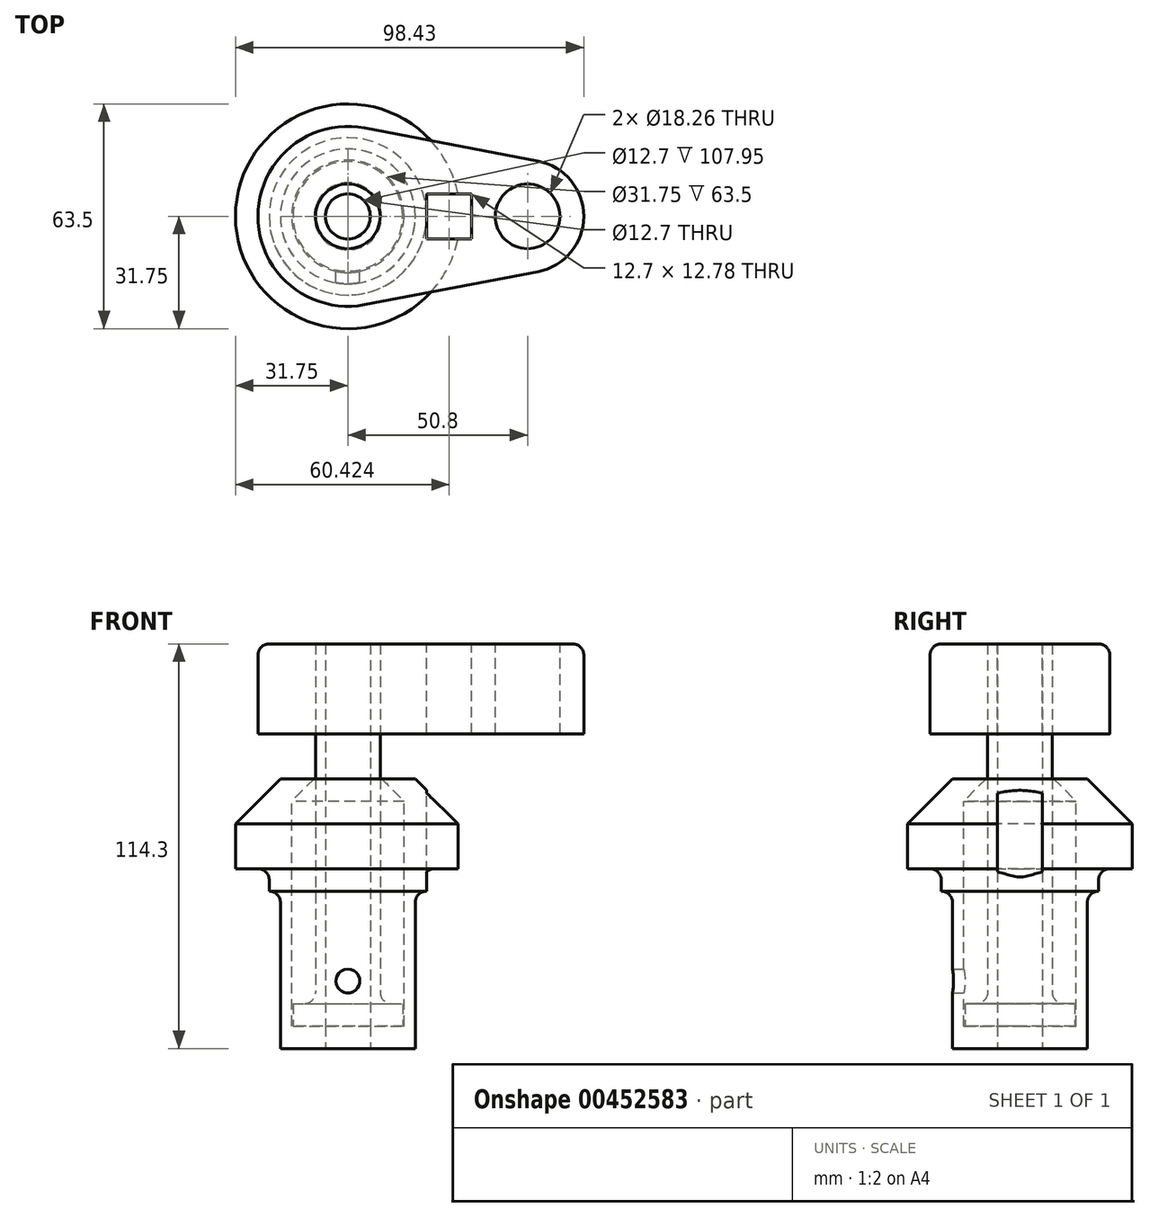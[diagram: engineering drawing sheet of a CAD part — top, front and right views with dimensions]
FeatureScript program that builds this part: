
annotation { "Feature Type Name" : "Feature", "Feature Type Description" : "" }
export const myFeature = defineFeature(function(context is Context, id is Id, definition is map)
    precondition{}
    {
        {
            var Q0;
            Q0=qCreatedBy(makeId("Front.planeOp"),FACE);
            var sketch = newSketch(context, id + "F0", { "sketchPlane" : qUnion([Q0])});
            skLineSegment(sketch, "E0", {"start": v(0, 0) * mm, "end": v(0, 76.2) * mm});
            skLineSegment(sketch, "E1", {"start": v(0, 76.2) * mm, "end": v(19.05, 76.2) * mm});
            skLineSegment(sketch, "E2", {"start": v(19.05, 76.2) * mm, "end": v(31.75, 63.5) * mm});
            skLineSegment(sketch, "E3", {"start": v(31.75, 63.5) * mm, "end": v(31.75, 50.8) * mm});
            skLineSegment(sketch, "E4", {"start": v(31.75, 50.8) * mm, "end": v(22.23, 50.8) * mm});
            skLineSegment(sketch, "E5", {"start": v(22.23, 50.8) * mm, "end": v(22.23, 44.45) * mm});
            skLineSegment(sketch, "E6", {"start": v(22.23, 44.45) * mm, "end": v(19.05, 44.45) * mm});
            skLineSegment(sketch, "E7", {"start": v(19.05, 44.45) * mm, "end": v(19.05, 0) * mm});
            skLineSegment(sketch, "E8", {"start": v(19.05, 0) * mm, "end": v(0, 0) * mm});
            skLineSegment(sketch, "E9", {"start": v(9.52, 76.2) * mm, "end": v(15.88, 69.85) * mm});
            skLineSegment(sketch, "E10", {"start": v(15.88, 69.85) * mm, "end": v(15.88, 6.35) * mm});
            skLineSegment(sketch, "E11", {"start": v(15.88, 6.35) * mm, "end": v(0, 6.35) * mm});
            skLineSegment(sketch, "E12", {"start": v(0, 76.2) * mm, "end": v(0, 96.2) * mm, "construction": true});
            skLineSegment(sketch, "E13", {"start": v(0, 76.2) * mm, "end": v(0, 114.3) * mm});
            skLineSegment(sketch, "E14", {"start": v(0, 114.3) * mm, "end": v(9.13, 114.3) * mm});
            skLineSegment(sketch, "E15", {"start": v(9.13, 114.3) * mm, "end": v(9.13, 12.7) * mm});
            skLineSegment(sketch, "E16", {"start": v(9.13, 12.7) * mm, "end": v(15.48, 12.7) * mm});
            skLineSegment(sketch, "E17", {"start": v(15.48, 12.7) * mm, "end": v(15.48, 6.35) * mm});
            skSolve(sketch);
        }
        {
            var Q0;
            {var subQ4=sQuery(id+"F0.wireOp",EDGE,"E2");Q0=makeQuery(id+"F0.imprint","IMPRINT",FACE,{"disambiguationData":[TD([[makeQuery(id+"F0.imprint","IMPRINT",EDGE,{"derivedFrom":subQ4}),-1.0]])]});}
            var Q1;
            Q1=sQuery(id+"F0.wireOp",EDGE,"E0");
            revolve(context, id + "F1", {"entities" : qUnion([Q0]), "axis" : qUnion([Q1]), "revolveType" : RevolveType.FULL, "oppositeDirection" : true});
        }
        {
            var Q0;
            {var subQ0=sQuery(id+"F0.wireOp",EDGE,"E13");Q0=makeQuery(id+"F0.imprint","IMPRINT",FACE,{"disambiguationData":[TD([[makeQuery(id+"F0.imprint","IMPRINT",EDGE,{"derivedFrom":subQ0}),-1.0]])]});}
            var Q1;
            {var subQ0=sQuery(id+"F0.wireOp",EDGE,"E16");Q1=makeQuery(id+"F0.imprint","IMPRINT",FACE,{"disambiguationData":[TD([[makeQuery(id+"F0.imprint","IMPRINT",EDGE,{"derivedFrom":subQ0}),-1.0]])]});}
            var Q2;
            Q2=sQuery(id+"F0.wireOp",EDGE,"E13");
            revolve(context, id + "F2", {"entities" : qUnion([Q0, Q1]), "axis" : qUnion([Q2]), "revolveType" : RevolveType.FULL});
        }
        {
            var Q0;
            Q0=makeQuery(id+"F2.opRevolve","SWEPT_FACE",FACE,{"disambiguationData":[OSD([sQuery(id+"F0.wireOp",EDGE,"E14")])]});
            var sketch = newSketch(context, id + "F3", { "sketchPlane" : qUnion([Q0])});
            skCircle(sketch, "E18", {"center": v(0, 0) * mm, "radius": 25.4 * mm});
            skCircle(sketch, "E19", {"center": v(50.8, 0) * mm, "radius": 15.88 * mm});
            skLineSegment(sketch, "E20", {"start": v(53.78, 15.6) * mm, "end": v(4.76, 24.95) * mm});
            skLineSegment(sketch, "E21", {"start": v(4.76, -24.95) * mm, "end": v(53.78, -15.6) * mm});
            skCircle(sketch, "E22.0", {"center": v(0, 0) * mm, "radius": 9.13 * mm});
            skCircle(sketch, "E23", {"center": v(50.8, 0) * mm, "radius": 9.13 * mm});
            skSolve(sketch);
        }
        {
            var Q0;
            Q0 = qSketchRegion(id + "F3", true);
            var Q1;
            Q1=makeQuery(id+"F1.opRevolve","SWEPT_FACE",FACE,{"disambiguationData":[OSD([sQuery(id+"F0.wireOp",EDGE,"E1")])]});
            extrude(context, id + "F4", {"entities" : qUnion([Q0]), "oppositeDirection" : true, "endBoundEntityFace" : qUnion([Q1]), "depth" : 25.4 * mm});
        }
        {
            var Q0;
            Q0=qCreatedBy(makeId("Front.planeOp"),FACE);
            var sketch = newSketch(context, id + "F5", { "sketchPlane" : qUnion([Q0])});
            skPoint(sketch, "E24", {"position": v(0, 19.05) * mm});
            skSolve(sketch);
        }
        {
            var Q0;
            Q0=sQuery(id+"F5.wireOp",VERTEX,"E24");
            var Q1;
            Q1=makeQuery(id+"F1.opRevolve","SWEPT_BODY",BODY,{"disambiguationData":[OSD([sQuery(id+"F0.wireOp",EDGE,"E0"),sQuery(id+"F0.wireOp",EDGE,"E1"),sQuery(id+"F0.wireOp",EDGE,"E2"),sQuery(id+"F0.wireOp",EDGE,"E3"),sQuery(id+"F0.wireOp",EDGE,"E4"),sQuery(id+"F0.wireOp",EDGE,"E5"),sQuery(id+"F0.wireOp",EDGE,"E6"),sQuery(id+"F0.wireOp",EDGE,"E7"),sQuery(id+"F0.wireOp",EDGE,"E8"),sQuery(id+"F0.wireOp",EDGE,"E9"),sQuery(id+"F0.wireOp",EDGE,"E10"),sQuery(id+"F0.wireOp",EDGE,"E11")])]});
            hole(context, id + "F6", {"style" : HoleStyle.SIMPLE, "endStyle" : HoleEndStyle.THROUGH, "oppositeDirection" : true, "standardTappedOrClearance" : lookupTablePath({ "standard" : "ANSI", "fit" : "Normal (ASME)", "size" : "1/4", "type" : "Clearance" }), "standardBlindInLast" : lookupTablePath({ "fit" : "Free", "standard" : "ANSI", "size" : "1/4", "type" : "Clearance" }), "holeDiameter" : 6.76 * mm, "tappedDepth" : 14.3 * mm, "tapClearance" : 3, "locations" : qUnion([Q0]), "scope" : qUnion([Q1])});
        }
        {
            var Q0;
            Q0=makeQuery(id+"F4.opExtrude","CAP_EDGE",EDGE,{"disambiguationData":[OSD([sQuery(id+"F3.wireOp",EDGE,"E20")])],"isStart":true});
            var Q1;
            Q1=makeQuery(id+"F1.opRevolve","SWEPT_EDGE",EDGE,{"disambiguationData":[OSD([sQuery(id+"F0.wireOp",EDGE,"E6"),sQuery(id+"F0.wireOp",EDGE,"E7")])]});
            var Q2;
            Q2=makeQuery(id+"F1.opRevolve","SWEPT_EDGE",EDGE,{"disambiguationData":[OSD([sQuery(id+"F0.wireOp",EDGE,"E4"),sQuery(id+"F0.wireOp",EDGE,"E5")])]});
            var Q3;
            Q3=makeQuery(id+"F2.opRevolve","SWEPT_EDGE",EDGE,{"disambiguationData":[OSD([sQuery(id+"F0.wireOp",EDGE,"E15"),sQuery(id+"F0.wireOp",EDGE,"E16")])]});
            fillet(context, id + "F7", {"entities" : qUnion([Q0, Q1, Q2, Q3]), "radius" : 3.17 * mm, "tangentPropagation" : true, "allowEdgeOverflow" : false});
        }
        {
            var Q0;
            Q0=makeQuery(id+"F1.opRevolve","SWEPT_FACE",FACE,{"disambiguationData":[OSD([sQuery(id+"F0.wireOp",EDGE,"E8")])]});
            var sketch = newSketch(context, id + "F8", { "sketchPlane" : qUnion([Q0])});
            skCircle(sketch, "E25", {"center": v(0, 0) * mm, "radius": 6.35 * mm});
            skSolve(sketch);
        }
        {
            var Q0;
            Q0=makeQuery(id+"F8.imprint","IMPRINT",FACE,{"disambiguationData":[TD([[makeQuery(id+"F8.imprint","IMPRINT",EDGE,{"derivedFrom":sQuery(id+"F8.wireOp",EDGE,"E25")}),1.0]])]});
            extrude(context, id + "F9", {"entities" : qUnion([Q0]), "operationType" : NewBodyOperationType.REMOVE, "endBound" : BoundingType.THROUGH_ALL, "oppositeDirection" : true, "depth" : 25.4 * mm});
        }
        {
            var Q0;
            Q0=makeQuery(id+"F4.opExtrude","CAP_FACE",FACE,{"disambiguationData":[OSD([sQuery(id+"F3.wireOp",EDGE,"E18"),sQuery(id+"F3.wireOp",EDGE,"E19"),sQuery(id+"F3.wireOp",EDGE,"E20"),sQuery(id+"F3.wireOp",EDGE,"E21"),sQuery(id+"F3.wireOp",EDGE,"E22.0"),sQuery(id+"F3.wireOp",EDGE,"E23")])],"isStart":true});
            var sketch = newSketch(context, id + "F10", { "sketchPlane" : qUnion([Q0])});
            skLineSegment(sketch, "E26.bottom", {"start": v(35.02, -6.39) * mm, "end": v(22.32, -6.39) * mm});
            skLineSegment(sketch, "E26.top", {"start": v(35.02, 6.39) * mm, "end": v(22.32, 6.39) * mm});
            skLineSegment(sketch, "E26.left", {"start": v(35.02, -6.39) * mm, "end": v(35.02, 6.39) * mm});
            skLineSegment(sketch, "E26.right", {"start": v(22.32, -6.39) * mm, "end": v(22.32, 6.39) * mm});
            skPoint(sketch, "E26.middle", {"position": v(28.67, 0) * mm});
            skPoint(sketch, "E26.middle.positionSnap0", {"position": v(28.67, 17.15) * mm});
            skPoint(sketch, "E26.centerSnap0", {"position": v(28.67, 17.15) * mm});
            skSolve(sketch);
        }
        {
            var Q0;
            Q0 = qSketchRegion(id + "F10", true);
            extrude(context, id + "F11", {"entities" : qUnion([Q0]), "operationType" : NewBodyOperationType.REMOVE, "endBound" : BoundingType.THROUGH_ALL, "oppositeDirection" : true, "depth" : 25.4 * mm});
        }
    });
